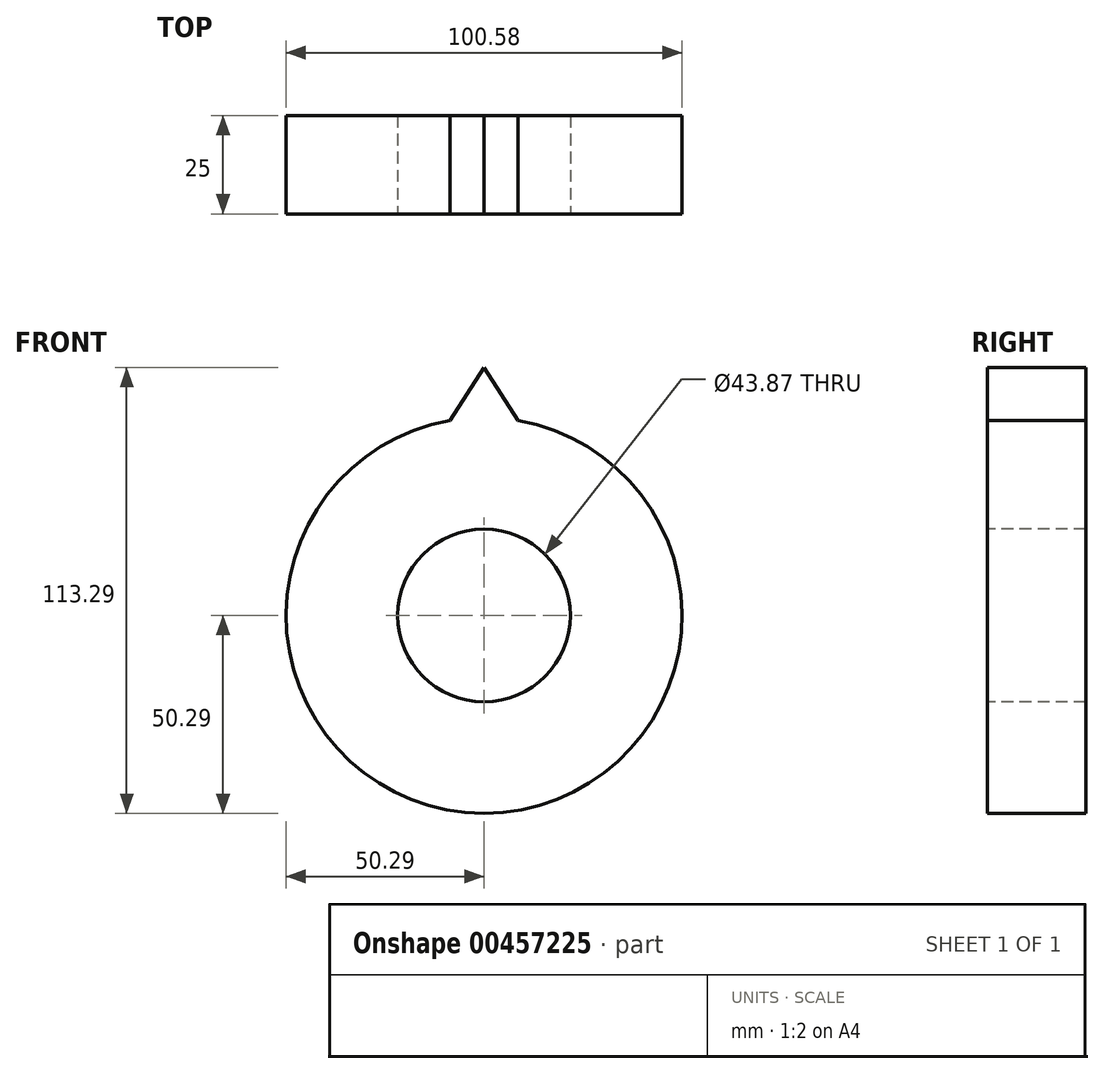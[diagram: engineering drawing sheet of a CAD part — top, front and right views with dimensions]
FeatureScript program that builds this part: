
annotation { "Feature Type Name" : "Feature", "Feature Type Description" : "" }
export const myFeature = defineFeature(function(context is Context, id is Id, definition is map)
    precondition{}
    {
        {
            var Q0;
            Q0=qCreatedBy(makeId("Front.planeOp"),FACE);
            var sketch = newSketch(context, id + "F0", { "sketchPlane" : qUnion([Q0])});
            skCircle(sketch, "E0", {"center": v(0, 0) * mm, "radius": 50.3 * mm});
            skSolve(sketch);
        }
        {
            var Q0;
            Q0 = qSketchRegion(id + "F0", true);
            extrude(context, id + "F1", {"entities" : qUnion([Q0]), "depth" : 25 * mm});
        }
        {
            var Q0;
            Q0=makeQuery(id+"F1.opExtrude","CAP_FACE",FACE,{"disambiguationData":[OSD([sQuery(id+"F0.wireOp",EDGE,"E0")])],"isStart":false});
            var sketch = newSketch(context, id + "F2", { "sketchPlane" : qUnion([Q0])});
            skCircle(sketch, "E1", {"center": v(0, 0) * mm, "radius": 21.94 * mm});
            skSolve(sketch);
        }
        {
            var Q0;
            Q0 = qSketchRegion(id + "F2", true);
            extrude(context, id + "F3", {"entities" : qUnion([Q0]), "operationType" : NewBodyOperationType.REMOVE, "oppositeDirection" : true, "depth" : 25 * mm});
        }
        {
            var Q0;
            Q0=qCreatedBy(makeId("Front.planeOp"),FACE);
            var sketch = newSketch(context, id + "F4", { "sketchPlane" : qUnion([Q0])});
            skLineSegment(sketch, "E2", {"start": v(-8.66, 49.54) * mm, "end": v(0, 63) * mm});
            skLineSegment(sketch, "E3", {"start": v(0, 63) * mm, "end": v(8.66, 49.54) * mm});
            skCircle(sketch, "E4.0", {"center": v(0, 0) * mm, "radius": 50.3 * mm});
            skSolve(sketch);
        }
        {
            var Q0;
            {var subQ0=sQuery(id+"F4.wireOp",EDGE,"E2");Q0=makeQuery(id+"F4.imprint","IMPRINT",FACE,{"disambiguationData":[TD([[makeQuery(id+"F4.imprint","IMPRINT",EDGE,{"derivedFrom":subQ0}),-1.0]])]});}
            extrude(context, id + "F5", {"entities" : qUnion([Q0]), "operationType" : NewBodyOperationType.ADD, "depth" : 25 * mm});
        }
    });
